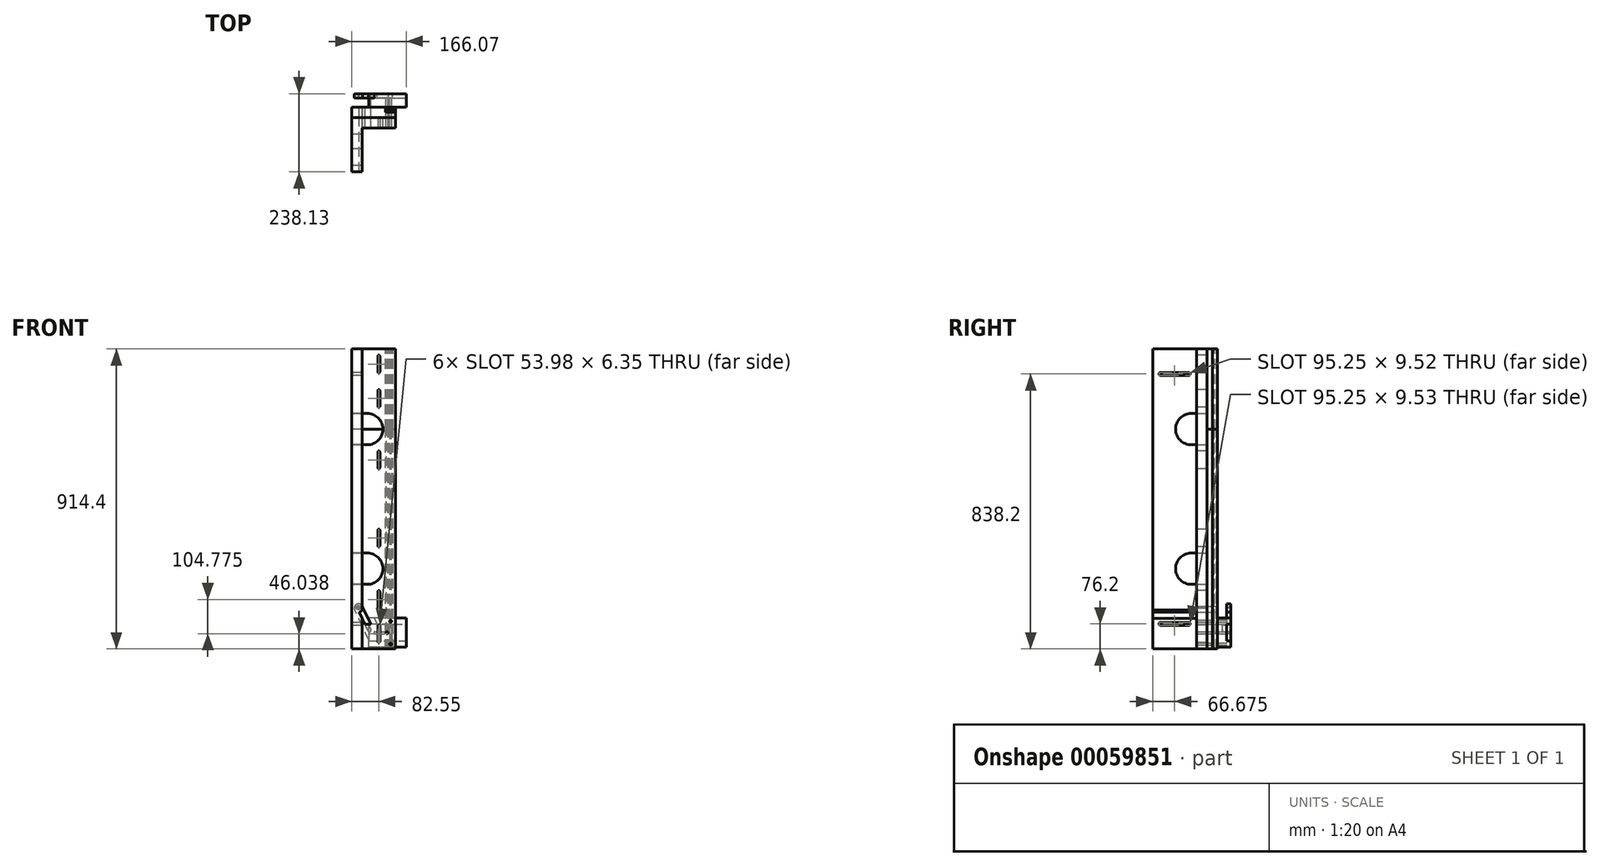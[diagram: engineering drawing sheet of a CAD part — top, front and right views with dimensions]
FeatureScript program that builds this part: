
annotation { "Feature Type Name" : "Feature", "Feature Type Description" : "" }
export const myFeature = defineFeature(function(context is Context, id is Id, definition is map)
    precondition{}
    {
        {
            var Q0;
            Q0=qCreatedBy(makeId("Top.planeOp"),FACE);
            var sketch = newSketch(context, id + "F0", { "sketchPlane" : qUnion([Q0])});
            skLineSegment(sketch, "E0", {"start": v(0, 0) * mm, "end": v(0, 165.1) * mm});
            skLineSegment(sketch, "E1", {"start": v(0, 165.1) * mm, "end": v(133.35, 165.1) * mm});
            skLineSegment(sketch, "E2.0", {"start": v(31.75, 133.35) * mm, "end": v(133.35, 133.35) * mm});
            skLineSegment(sketch, "E3.0", {"start": v(31.75, 0) * mm, "end": v(31.75, 133.35) * mm});
            skLineSegment(sketch, "E4", {"start": v(133.35, 133.35) * mm, "end": v(133.35, 165.1) * mm});
            skLineSegment(sketch, "E5", {"start": v(31.75, 0) * mm, "end": v(0, 0) * mm});
            skSolve(sketch);
        }
        {
            var Q0;
            Q0=makeQuery(id+"F0.imprint","IMPRINT",FACE,{"disambiguationData":[TD([[makeQuery(id+"F0.imprint","IMPRINT",EDGE,{"derivedFrom":sQuery(id+"F0.wireOp",EDGE,"E0")}),-1.0]])]});
            extrude(context, id + "F1", {"entities" : qUnion([Q0]), "depth" : 914.4 * mm});
        }
        {
            var Q0;
            Q0=makeQuery(id+"F1.opExtrude","SWEPT_FACE",FACE,{"disambiguationData":[OSD([sQuery(id+"F0.wireOp",EDGE,"E1")])]});
            var sketch = newSketch(context, id + "F2", { "sketchPlane" : qUnion([Q0])});
            skLineSegment(sketch, "E6", {"start": v(0, 196.85) * mm, "end": v(-47.63, 196.85) * mm});
            skLineSegment(sketch, "E7", {"start": v(0, 292.1) * mm, "end": v(-47.63, 292.1) * mm});
            skLineSegment(sketch, "E8", {"start": v(0, 196.85) * mm, "end": v(0, 292.1) * mm});
            skArc(sketch, "E9", {"start": v(-47.63, 196.85) * mm, "mid": v(-95.25, 244.48) * mm, "end": v(-47.63, 292.1) * mm});
            skLineSegment(sketch, "E10", {"start": v(0, 457.2) * mm, "end": v(-175.32, 457.2) * mm, "construction": true});
            skLineSegment(sketch, "E11.MirrorCS", {"start": v(0, 717.55) * mm, "end": v(-47.63, 717.55) * mm});
            skLineSegment(sketch, "E12.MirrorCS", {"start": v(0, 622.3) * mm, "end": v(-47.63, 622.3) * mm});
            skLineSegment(sketch, "E13.MirrorCS", {"start": v(0, 717.55) * mm, "end": v(0, 622.3) * mm});
            skArc(sketch, "E14.MirrorCS", {"start": v(-47.63, 717.55) * mm, "mid": v(-95.25, 669.93) * mm, "end": v(-47.63, 622.3) * mm});
            skSolve(sketch);
        }
        {
            var Q0;
            Q0 = qSketchRegion(id + "F2", true);
            var Q1;
            Q1=makeQuery(id+"F1.opExtrude","SWEPT_FACE",FACE,{"disambiguationData":[OSD([sQuery(id+"F0.wireOp",EDGE,"E2.0")])]});
            extrude(context, id + "F3", {"entities" : qUnion([Q0]), "operationType" : NewBodyOperationType.REMOVE, "endBound" : BoundingType.UP_TO_SURFACE, "oppositeDirection" : true, "endBoundEntityFace" : qUnion([Q1]), "depth" : 25.4 * mm});
        }
        {
            var Q0;
            Q0=makeQuery(id+"F1.opExtrude","SWEPT_FACE",FACE,{"disambiguationData":[OSD([sQuery(id+"F0.wireOp",EDGE,"E0")])]});
            var sketch = newSketch(context, id + "F4", { "sketchPlane" : qUnion([Q0])});
            skLineSegment(sketch, "E15", {"start": v(-165.1, 196.85) * mm, "end": v(-117.48, 196.85) * mm});
            skLineSegment(sketch, "E16", {"start": v(-165.1, 292.1) * mm, "end": v(-117.48, 292.1) * mm});
            skPoint(sketch, "E16.endSnap0", {"position": v(-149.22, 292.1) * mm});
            skLineSegment(sketch, "E17", {"start": v(-165.1, 196.85) * mm, "end": v(-165.1, 292.1) * mm});
            skArc(sketch, "E18", {"start": v(-117.48, 196.85) * mm, "mid": v(-69.85, 244.48) * mm, "end": v(-117.48, 292.1) * mm});
            skLineSegment(sketch, "E19", {"start": v(0, 457.2) * mm, "end": v(-264.31, 457.2) * mm, "construction": true});
            skArc(sketch, "E20.MirrorCS", {"start": v(-117.48, 717.55) * mm, "mid": v(-69.85, 669.93) * mm, "end": v(-117.48, 622.3) * mm});
            skLineSegment(sketch, "E21.MirrorCS", {"start": v(-165.1, 717.55) * mm, "end": v(-165.1, 622.3) * mm});
            skLineSegment(sketch, "E22.MirrorCS", {"start": v(-165.1, 622.3) * mm, "end": v(-117.48, 622.3) * mm});
            skLineSegment(sketch, "E23.MirrorCS", {"start": v(-165.1, 717.55) * mm, "end": v(-117.48, 717.55) * mm});
            skPoint(sketch, "E24.MirrorP", {"position": v(-149.22, 622.3) * mm});
            skSolve(sketch);
        }
        {
            var Q0;
            Q0 = qSketchRegion(id + "F4", true);
            var Q1;
            Q1=makeQuery(id+"F1.opExtrude","SWEPT_FACE",FACE,{"disambiguationData":[OSD([sQuery(id+"F0.wireOp",EDGE,"E3.0")])]});
            extrude(context, id + "F5", {"entities" : qUnion([Q0]), "operationType" : NewBodyOperationType.REMOVE, "endBound" : BoundingType.UP_TO_SURFACE, "oppositeDirection" : true, "endBoundEntityFace" : qUnion([Q1]), "depth" : 25.4 * mm});
        }
        {
            var Q0;
            Q0=makeQuery(id+"F1.opExtrude","SWEPT_FACE",FACE,{"disambiguationData":[OSD([sQuery(id+"F0.wireOp",EDGE,"E0")])]});
            var sketch = newSketch(context, id + "F6", { "sketchPlane" : qUnion([Q0])});
            skLineSegment(sketch, "E25.bottom", {"start": v(-109.54, 71.44) * mm, "end": v(-23.81, 71.44) * mm});
            skLineSegment(sketch, "E25.top", {"start": v(-109.54, 80.96) * mm, "end": v(-23.81, 80.96) * mm});
            skArc(sketch, "E26", {"start": v(-109.54, 80.96) * mm, "mid": v(-114.3, 76.2) * mm, "end": v(-109.54, 71.44) * mm});
            skArc(sketch, "E27", {"start": v(-23.81, 71.44) * mm, "mid": v(-19.05, 76.2) * mm, "end": v(-23.81, 80.96) * mm});
            skLineSegment(sketch, "E28.MirrorCS", {"start": v(-109.54, 842.96) * mm, "end": v(-23.81, 842.96) * mm});
            skLineSegment(sketch, "E29.MirrorCS", {"start": v(-109.54, 833.44) * mm, "end": v(-23.81, 833.44) * mm});
            skArc(sketch, "E30.MirrorCS", {"start": v(-109.54, 833.44) * mm, "mid": v(-114.3, 838.2) * mm, "end": v(-109.54, 842.96) * mm});
            skArc(sketch, "E31.MirrorCS", {"start": v(-23.81, 842.96) * mm, "mid": v(-19.05, 838.2) * mm, "end": v(-23.81, 833.44) * mm});
            skSolve(sketch);
        }
        {
            var Q0;
            Q0 = qSketchRegion(id + "F6", true);
            extrude(context, id + "F7", {"entities" : qUnion([Q0]), "operationType" : NewBodyOperationType.REMOVE, "endBound" : BoundingType.THROUGH_ALL, "oppositeDirection" : true, "depth" : 25.4 * mm});
        }
        {
            var Q0;
            Q0=makeQuery(id+"F1.opExtrude","SWEPT_FACE",FACE,{"disambiguationData":[OSD([sQuery(id+"F0.wireOp",EDGE,"E2.0")])]});
            var sketch = newSketch(context, id + "F8", { "sketchPlane" : qUnion([Q0])});
            skLineSegment(sketch, "E32.left", {"start": v(85.73, 22.23) * mm, "end": v(85.72, 69.85) * mm});
            skLineSegment(sketch, "E32.right", {"start": v(79.38, 22.23) * mm, "end": v(79.37, 69.85) * mm});
            skArc(sketch, "E33", {"start": v(79.38, 22.23) * mm, "mid": v(82.55, 19.05) * mm, "end": v(85.73, 22.23) * mm});
            skArc(sketch, "E34", {"start": v(85.73, 69.85) * mm, "mid": v(82.55, 73.02) * mm, "end": v(79.38, 69.85) * mm});
            skLineSegment(sketch, "E35", {"start": v(82.55, 0) * mm, "end": v(82.55, 223.18) * mm, "construction": true});
            skLineSegment(sketch, "E36", {"start": v(31.75, 98.43) * mm, "end": v(177.99, 98.43) * mm, "construction": true});
            skLineSegment(sketch, "E37.MirrorCS", {"start": v(85.73, 174.63) * mm, "end": v(85.72, 127) * mm});
            skArc(sketch, "E38.MirrorCS", {"start": v(85.73, 127) * mm, "mid": v(82.55, 123.83) * mm, "end": v(79.38, 127) * mm});
            skArc(sketch, "E39.MirrorCS", {"start": v(79.38, 174.63) * mm, "mid": v(82.55, 177.8) * mm, "end": v(85.73, 174.63) * mm});
            skLineSegment(sketch, "E40.MirrorCS", {"start": v(79.38, 174.63) * mm, "end": v(79.37, 127) * mm});
            skLineSegment(sketch, "E41", {"start": v(47.63, 244.48) * mm, "end": v(193.78, 244.47) * mm, "construction": true});
            skArc(sketch, "E42.MirrorCS", {"start": v(79.38, 314.32) * mm, "mid": v(82.55, 311.15) * mm, "end": v(85.73, 314.32) * mm});
            skArc(sketch, "E43.MirrorCS", {"start": v(85.73, 361.95) * mm, "mid": v(82.55, 365.12) * mm, "end": v(79.38, 361.95) * mm});
            skLineSegment(sketch, "E44.MirrorCS", {"start": v(79.38, 314.32) * mm, "end": v(79.38, 361.95) * mm});
            skLineSegment(sketch, "E45.MirrorCS", {"start": v(85.73, 314.32) * mm, "end": v(85.73, 361.95) * mm});
            skArc(sketch, "E46.MirrorCS", {"start": v(85.73, 787.4) * mm, "mid": v(82.55, 790.57) * mm, "end": v(79.38, 787.4) * mm});
            skArc(sketch, "E47.MirrorCS", {"start": v(85.73, 552.45) * mm, "mid": v(82.55, 549.28) * mm, "end": v(79.38, 552.45) * mm});
            skArc(sketch, "E48.MirrorCS", {"start": v(79.38, 600.08) * mm, "mid": v(82.55, 603.25) * mm, "end": v(85.73, 600.08) * mm});
            skArc(sketch, "E49.MirrorCS", {"start": v(79.38, 892.18) * mm, "mid": v(82.55, 895.35) * mm, "end": v(85.73, 892.18) * mm});
            skArc(sketch, "E50.MirrorCS", {"start": v(79.38, 739.78) * mm, "mid": v(82.55, 736.6) * mm, "end": v(85.73, 739.78) * mm});
            skArc(sketch, "E51.MirrorCS", {"start": v(85.73, 844.55) * mm, "mid": v(82.55, 841.38) * mm, "end": v(79.38, 844.55) * mm});
            skLineSegment(sketch, "E52.MirrorCS", {"start": v(79.38, 739.78) * mm, "end": v(79.37, 787.4) * mm});
            skLineSegment(sketch, "E53.MirrorCS", {"start": v(79.38, 600.08) * mm, "end": v(79.38, 552.45) * mm});
            skLineSegment(sketch, "E54.MirrorCS", {"start": v(85.73, 600.08) * mm, "end": v(85.73, 552.45) * mm});
            skLineSegment(sketch, "E55.MirrorCS", {"start": v(85.73, 892.18) * mm, "end": v(85.72, 844.55) * mm});
            skLineSegment(sketch, "E56.MirrorCS", {"start": v(79.38, 892.18) * mm, "end": v(79.37, 844.55) * mm});
            skLineSegment(sketch, "E57.MirrorCS", {"start": v(85.73, 739.78) * mm, "end": v(85.72, 787.4) * mm});
            skSolve(sketch);
        }
        {
            var Q0;
            Q0 = qSketchRegion(id + "F8", true);
            extrude(context, id + "F9", {"entities" : qUnion([Q0]), "operationType" : NewBodyOperationType.REMOVE, "endBound" : BoundingType.THROUGH_ALL, "oppositeDirection" : true, "depth" : 25.4 * mm});
        }
        {
            var Q0;
            {var subQ4=sQuery(id+"F2.wireOp",EDGE,"E6");Q0=makeQuery(id+"F2.imprint","IMPRINT",FACE,{"disambiguationData":[TD([[makeQuery(id+"F2.imprint","IMPRINT",EDGE,{"derivedFrom":subQ4}),1.0]])]});}
            var sketch = newSketch(context, id + "F10", { "sketchPlane" : qUnion([Q0])});
            skLineSegment(sketch, "E58.bottom", {"start": v(-133.35, 914.4) * mm, "end": v(0, 914.4) * mm});
            skLineSegment(sketch, "E58.top", {"start": v(-133.35, 669.93) * mm, "end": v(0, 669.93) * mm});
            skLineSegment(sketch, "E58.left", {"start": v(-133.35, 914.4) * mm, "end": v(-133.35, 669.93) * mm});
            skLineSegment(sketch, "E58.right", {"start": v(0, 914.4) * mm, "end": v(0, 669.93) * mm});
            skSolve(sketch);
        }
        {
            var Q0;
            Q0 = qSketchRegion(id + "F10", true);
            extrude(context, id + "F11", {"entities" : qUnion([Q0]), "depth" : 31.75 * mm});
        }
        {
            var Q0;
            {var subQ4=sQuery(id+"F2.wireOp",EDGE,"E6");Q0=makeQuery(id+"F2.imprint","IMPRINT",FACE,{"disambiguationData":[TD([[makeQuery(id+"F2.imprint","IMPRINT",EDGE,{"derivedFrom":subQ4}),1.0]])]});}
            var sketch = newSketch(context, id + "F12", { "sketchPlane" : qUnion([Q0])});
            skLineSegment(sketch, "E59.bottom", {"start": v(-133.35, 669.93) * mm, "end": v(0, 669.93) * mm});
            skLineSegment(sketch, "E59.top", {"start": v(-133.35, 0) * mm, "end": v(0, 0) * mm});
            skLineSegment(sketch, "E59.left", {"start": v(-133.35, 669.93) * mm, "end": v(-133.35, 0) * mm});
            skLineSegment(sketch, "E59.right", {"start": v(0, 669.93) * mm, "end": v(0, 0) * mm});
            skSolve(sketch);
        }
        {
            var Q0;
            Q0 = qSketchRegion(id + "F12", true);
            extrude(context, id + "F13", {"entities" : qUnion([Q0]), "depth" : 31.75 * mm});
        }
        {
            var Q0;
            Q0=makeQuery(id+"F11.opExtrude","SWEPT_FACE",FACE,{"disambiguationData":[OSD([sQuery(id+"F10.wireOp",EDGE,"E58.bottom")])]});
            var sketch = newSketch(context, id + "F14", { "sketchPlane" : qUnion([Q0])});
            skLineSegment(sketch, "E60.bottom", {"start": v(133.35, 196.85) * mm, "end": v(103.53, 196.85) * mm});
            skLineSegment(sketch, "E60.top", {"start": v(133.35, 182.14) * mm, "end": v(103.53, 182.14) * mm});
            skLineSegment(sketch, "E60.left", {"start": v(133.35, 196.85) * mm, "end": v(133.35, 182.14) * mm});
            skLineSegment(sketch, "E60.right", {"start": v(103.53, 196.85) * mm, "end": v(103.53, 182.14) * mm});
            skSolve(sketch);
        }
        {
            var Q0;
            Q0 = qSketchRegion(id + "F14", true);
            extrude(context, id + "F15", {"entities" : qUnion([Q0]), "operationType" : NewBodyOperationType.REMOVE, "endBound" : BoundingType.THROUGH_ALL, "oppositeDirection" : true, "depth" : 25.4 * mm});
        }
        {
            var Q0;
            Q0=makeQuery(id+"F13.opExtrude","SWEPT_FACE",FACE,{"disambiguationData":[OSD([sQuery(id+"F12.wireOp",EDGE,"E59.bottom")])]});
            var sketch = newSketch(context, id + "F16", { "sketchPlane" : qUnion([Q0])});
            skLineSegment(sketch, "E61.bottom", {"start": v(133.35, 196.85) * mm, "end": v(103.53, 196.85) * mm});
            skLineSegment(sketch, "E61.top", {"start": v(133.35, 182.14) * mm, "end": v(103.53, 182.14) * mm});
            skLineSegment(sketch, "E61.left", {"start": v(133.35, 196.85) * mm, "end": v(133.35, 182.14) * mm});
            skLineSegment(sketch, "E61.right", {"start": v(103.53, 196.85) * mm, "end": v(103.53, 182.14) * mm});
            skSolve(sketch);
        }
        {
            var Q0;
            Q0 = qSketchRegion(id + "F16", true);
            extrude(context, id + "F17", {"entities" : qUnion([Q0]), "operationType" : NewBodyOperationType.REMOVE, "endBound" : BoundingType.THROUGH_ALL, "oppositeDirection" : true, "depth" : 25.4 * mm});
        }
        {
            var Q0;
            Q0=makeQuery(id+"F11.opExtrude","SWEPT_FACE",FACE,{"disambiguationData":[OSD([sQuery(id+"F10.wireOp",EDGE,"E58.bottom")])]});
            var sketch = newSketch(context, id + "F18", { "sketchPlane" : qUnion([Q0])});
            skLineSegment(sketch, "E62", {"start": v(133.35, 182.14) * mm, "end": v(103.53, 182.14) * mm});
            skLineSegment(sketch, "E63", {"start": v(103.53, 182.14) * mm, "end": v(103.53, 196.85) * mm});
            skLineSegment(sketch, "E64", {"start": v(103.53, 196.85) * mm, "end": v(115.27, 196.85) * mm});
            skLineSegment(sketch, "E65", {"start": v(115.27, 196.85) * mm, "end": v(115.27, 195.07) * mm});
            skLineSegment(sketch, "E66", {"start": v(115.27, 195.07) * mm, "end": v(112.73, 195.07) * mm});
            skLineSegment(sketch, "E67", {"start": v(112.73, 195.07) * mm, "end": v(112.73, 188.72) * mm});
            skLineSegment(sketch, "E68", {"start": v(112.73, 188.72) * mm, "end": v(124.16, 188.72) * mm});
            skLineSegment(sketch, "E69", {"start": v(124.16, 188.72) * mm, "end": v(124.16, 195.07) * mm});
            skLineSegment(sketch, "E70", {"start": v(124.16, 195.07) * mm, "end": v(121.62, 195.07) * mm});
            skLineSegment(sketch, "E71", {"start": v(121.62, 195.07) * mm, "end": v(121.62, 196.85) * mm});
            skLineSegment(sketch, "E72", {"start": v(121.62, 196.85) * mm, "end": v(133.35, 196.85) * mm});
            skLineSegment(sketch, "E73", {"start": v(133.35, 196.85) * mm, "end": v(133.35, 182.14) * mm});
            skLineSegment(sketch, "E74", {"start": v(116.66, 183.92) * mm, "end": v(116.66, 186.94) * mm});
            skLineSegment(sketch, "E75", {"start": v(116.66, 186.94) * mm, "end": v(110.95, 186.94) * mm});
            skLineSegment(sketch, "E76", {"start": v(110.95, 186.94) * mm, "end": v(110.95, 195.07) * mm});
            skLineSegment(sketch, "E77", {"start": v(110.95, 195.07) * mm, "end": v(105.3, 195.07) * mm});
            skLineSegment(sketch, "E78", {"start": v(105.3, 195.07) * mm, "end": v(105.3, 183.92) * mm});
            skLineSegment(sketch, "E79", {"start": v(105.3, 183.92) * mm, "end": v(116.66, 183.92) * mm});
            skLineSegment(sketch, "E80", {"start": v(118.44, 182.14) * mm, "end": v(118.44, 192.35) * mm, "construction": true});
            skLineSegment(sketch, "E81.MirrorCS", {"start": v(120.22, 183.92) * mm, "end": v(120.22, 186.94) * mm});
            skLineSegment(sketch, "E82.MirrorCS", {"start": v(120.22, 186.94) * mm, "end": v(125.93, 186.94) * mm});
            skLineSegment(sketch, "E83.MirrorCS", {"start": v(131.57, 183.92) * mm, "end": v(120.22, 183.92) * mm});
            skLineSegment(sketch, "E84.MirrorCS", {"start": v(125.93, 186.94) * mm, "end": v(125.93, 195.07) * mm});
            skLineSegment(sketch, "E85.MirrorCS", {"start": v(131.57, 195.07) * mm, "end": v(131.57, 183.92) * mm});
            skLineSegment(sketch, "E86.MirrorCS", {"start": v(125.93, 195.07) * mm, "end": v(131.57, 195.07) * mm});
            skSolve(sketch);
        }
        {
            var Q0;
            Q0=makeQuery(id+"F18.imprint","IMPRINT",FACE,{"disambiguationData":[TD([[makeQuery(id+"F18.imprint","IMPRINT",EDGE,{"derivedFrom":sQuery(id+"F18.wireOp",EDGE,"E62")}),-1.0]])]});
            var Q1;
            Q1=makeQuery(id+"F11.opExtrude","SWEPT_FACE",FACE,{"disambiguationData":[OSD([sQuery(id+"F10.wireOp",EDGE,"E58.top")])]});
            extrude(context, id + "F19", {"entities" : qUnion([Q0]), "endBound" : BoundingType.UP_TO_SURFACE, "oppositeDirection" : true, "endBoundEntityFace" : qUnion([Q1]), "depth" : 79.93 * mm});
        }
        {
            var Q0;
            Q0=makeQuery(id+"F13.opExtrude","SWEPT_FACE",FACE,{"disambiguationData":[OSD([sQuery(id+"F12.wireOp",EDGE,"E59.bottom")])]});
            var sketch = newSketch(context, id + "F20", { "sketchPlane" : qUnion([Q0])});
            skLineSegment(sketch, "E87", {"start": v(133.35, 182.14) * mm, "end": v(103.53, 182.14) * mm});
            skLineSegment(sketch, "E88", {"start": v(103.53, 182.14) * mm, "end": v(103.53, 196.85) * mm});
            skLineSegment(sketch, "E89", {"start": v(103.53, 196.85) * mm, "end": v(115.27, 196.85) * mm});
            skLineSegment(sketch, "E90", {"start": v(115.27, 196.85) * mm, "end": v(115.27, 195.07) * mm});
            skLineSegment(sketch, "E91", {"start": v(115.27, 195.07) * mm, "end": v(112.73, 195.07) * mm});
            skLineSegment(sketch, "E92", {"start": v(112.73, 195.07) * mm, "end": v(112.73, 188.72) * mm});
            skLineSegment(sketch, "E93", {"start": v(112.73, 188.72) * mm, "end": v(124.16, 188.72) * mm});
            skLineSegment(sketch, "E94", {"start": v(124.16, 188.72) * mm, "end": v(124.16, 195.07) * mm});
            skLineSegment(sketch, "E95", {"start": v(124.16, 195.07) * mm, "end": v(121.62, 195.07) * mm});
            skLineSegment(sketch, "E96", {"start": v(121.62, 195.07) * mm, "end": v(121.62, 196.85) * mm});
            skLineSegment(sketch, "E97", {"start": v(121.62, 196.85) * mm, "end": v(133.35, 196.85) * mm});
            skLineSegment(sketch, "E98", {"start": v(133.35, 196.85) * mm, "end": v(133.35, 182.14) * mm});
            skLineSegment(sketch, "E99", {"start": v(116.66, 183.92) * mm, "end": v(116.66, 186.94) * mm});
            skLineSegment(sketch, "E100", {"start": v(116.66, 186.94) * mm, "end": v(110.95, 186.94) * mm});
            skLineSegment(sketch, "E101", {"start": v(110.95, 186.94) * mm, "end": v(110.95, 195.07) * mm});
            skLineSegment(sketch, "E102", {"start": v(110.95, 195.07) * mm, "end": v(105.3, 195.07) * mm});
            skLineSegment(sketch, "E103", {"start": v(105.3, 195.07) * mm, "end": v(105.3, 183.92) * mm});
            skLineSegment(sketch, "E104", {"start": v(105.3, 183.92) * mm, "end": v(116.66, 183.92) * mm});
            skLineSegment(sketch, "E105", {"start": v(118.44, 182.14) * mm, "end": v(118.44, 192.35) * mm, "construction": true});
            skLineSegment(sketch, "E106.MirrorCS", {"start": v(120.22, 183.92) * mm, "end": v(120.22, 186.94) * mm});
            skLineSegment(sketch, "E107.MirrorCS", {"start": v(120.22, 186.94) * mm, "end": v(125.93, 186.94) * mm});
            skLineSegment(sketch, "E108.MirrorCS", {"start": v(131.57, 183.92) * mm, "end": v(120.22, 183.92) * mm});
            skLineSegment(sketch, "E109.MirrorCS", {"start": v(125.93, 186.94) * mm, "end": v(125.93, 195.07) * mm});
            skLineSegment(sketch, "E110.MirrorCS", {"start": v(131.57, 195.07) * mm, "end": v(131.57, 183.92) * mm});
            skLineSegment(sketch, "E111.MirrorCS", {"start": v(125.93, 195.07) * mm, "end": v(131.57, 195.07) * mm});
            skSolve(sketch);
        }
        {
            var Q0;
            Q0 = qSketchRegion(id + "F20", true);
            var Q1;
            Q1=makeQuery(id+"F13.opExtrude","SWEPT_FACE",FACE,{"disambiguationData":[OSD([sQuery(id+"F12.wireOp",EDGE,"E59.top")])]});
            extrude(context, id + "F21", {"entities" : qUnion([Q0]), "endBound" : BoundingType.UP_TO_SURFACE, "oppositeDirection" : true, "endBoundEntityFace" : qUnion([Q1]), "depth" : 25.4 * mm});
        }
        {
            var Q0;
            Q0=makeQuery(id+"F21.opExtrude","SWEPT_FACE",FACE,{"disambiguationData":[OSD([sQuery(id+"F20.wireOp",EDGE,"E98")])]});
            cPlane(context, id + "F22", {"entities" : qUnion([Q0]), "cplaneType" : CPlaneType.OFFSET, "offset" : 14.9 * mm, "oppositeDirection" : true, "width" : 152.4 * mm, "height" : 152.4 * mm});
        }
        {
            var Q0;
            Q0=makeQuery(id+"F13.opExtrude","CAP_FACE",FACE,{"disambiguationData":[OSD([sQuery(id+"F12.wireOp",EDGE,"E59.bottom"),sQuery(id+"F12.wireOp",EDGE,"E59.top"),sQuery(id+"F12.wireOp",EDGE,"E59.left"),sQuery(id+"F12.wireOp",EDGE,"E59.right")])],"isStart":false});
            var sketch = newSketch(context, id + "F23", { "sketchPlane" : qUnion([Q0])});
            skLineSegment(sketch, "E112.bottom", {"start": v(-166.07, 4.91) * mm, "end": v(-51.77, 4.91) * mm});
            skLineSegment(sketch, "E112.top", {"start": v(-166.07, 93.81) * mm, "end": v(-51.77, 93.81) * mm});
            skLineSegment(sketch, "E112.left", {"start": v(-166.07, 4.91) * mm, "end": v(-166.07, 93.81) * mm});
            skLineSegment(sketch, "E112.right", {"start": v(-51.77, 4.91) * mm, "end": v(-51.77, 93.81) * mm});
            skSolve(sketch);
        }
        {
            var Q0;
            {var subQ0=sQuery(id+"F23.wireOp",EDGE,"E112.left");Q0=makeQuery(id+"F23.imprint","IMPRINT",FACE,{"disambiguationData":[TD([[makeQuery(id+"F23.imprint","IMPRINT",EDGE,{"derivedFrom":subQ0}),-1.0]])]});}
            var Q1;
            {var subQ0=sQuery(id+"F23.wireOp",EDGE,"E112.right");Q1=makeQuery(id+"F23.imprint","IMPRINT",FACE,{"disambiguationData":[TD([[makeQuery(id+"F23.imprint","IMPRINT",EDGE,{"derivedFrom":subQ0}),1.0]])]});}
            extrude(context, id + "F24", {"entities" : qUnion([Q0, Q1]), "depth" : 41.27 * mm});
        }
        {
            var Q0;
            Q0=makeQuery(id+"F24.opExtrude","SWEPT_FACE",FACE,{"disambiguationData":[OSD([sQuery(id+"F23.wireOp",EDGE,"E112.left")])]});
            var sketch = newSketch(context, id + "F25", { "sketchPlane" : qUnion([Q0])});
            skLineSegment(sketch, "E113.top", {"start": v(238.13, 23.96) * mm, "end": v(225.43, 23.96) * mm});
            skLineSegment(sketch, "E113.right", {"start": v(225.43, 74.76) * mm, "end": v(225.43, 23.96) * mm});
            skPoint(sketch, "E114.endSnap0", {"position": v(217.49, 93.81) * mm});
            skLineSegment(sketch, "E115", {"start": v(225.43, 74.76) * mm, "end": v(238.13, 74.76) * mm});
            skLineSegment(sketch, "E116", {"start": v(238.13, 49.36) * mm, "end": v(214.84, 49.36) * mm, "construction": true});
            skPoint(sketch, "E116.endSnap0", {"position": v(238.13, 49.36) * mm});
            skLineSegment(sketch, "E117", {"start": v(214.84, 49.36) * mm, "end": v(228.34, 49.36) * mm});
            skLineSegment(sketch, "E118", {"start": v(238.13, 23.96) * mm, "end": v(238.13, 49.36) * mm});
            skLineSegment(sketch, "E119", {"start": v(238.13, 74.76) * mm, "end": v(238.13, 49.36) * mm});
            skSolve(sketch);
        }
        {
            var Q0;
            Q0 = qSketchRegion(id + "F25", true);
            extrude(context, id + "F26", {"entities" : qUnion([Q0]), "operationType" : NewBodyOperationType.REMOVE, "endBound" : BoundingType.THROUGH_ALL, "oppositeDirection" : true, "depth" : 25.4 * mm});
        }
        {
            var Q0;
            Q0=makeQuery(id+"F24.opExtrude","CAP_FACE",FACE,{"disambiguationData":[OSD([sQuery(id+"F23.wireOp",EDGE,"E112.bottom"),sQuery(id+"F23.wireOp",EDGE,"E112.top"),sQuery(id+"F23.wireOp",EDGE,"E112.left"),sQuery(id+"F23.wireOp",EDGE,"E112.right")])],"isStart":false});
            var sketch = newSketch(context, id + "F27", { "sketchPlane" : qUnion([Q0])});
            skPoint(sketch, "E120.endSnap0", {"position": v(-51.77, 14.44) * mm});
            skCircle(sketch, "E121.MirrorC", {"center": v(-118.44, 14.44) * mm, "radius": 3.18 * mm});
            skLineSegment(sketch, "E122", {"start": v(-166.07, 14.44) * mm, "end": v(-75.74, 14.44) * mm, "construction": true});
            skPoint(sketch, "E122.endSnap0", {"position": v(-166.07, 14.44) * mm});
            skPoint(sketch, "E123.endSnap0", {"position": v(-108.92, 23.96) * mm});
            skSolve(sketch);
        }
        {
            var Q0;
            Q0 = qSketchRegion(id + "F27", true);
            extrude(context, id + "F28", {"entities" : qUnion([Q0]), "operationType" : NewBodyOperationType.REMOVE, "endBound" : BoundingType.THROUGH_ALL, "oppositeDirection" : true, "depth" : 25.4 * mm});
        }
        {
            var Q0;
            {var subQ0=sQuery(id+"F23.wireOp",EDGE,"E112.top");var subQ1=sQuery(id+"F23.wireOp",EDGE,"E112.left");var subQ2=sQuery(id+"F23.wireOp",EDGE,"E112.right");Q0=makeQuery(id+"F26.boolean.opBoolean","SPLIT",FACE,{"disambiguationData":[TD([makeQuery(id+"F24.opExtrude","SWEPT_FACE",FACE,{"disambiguationData":[OSD([subQ0])]})])],"derivedFrom":makeQuery(id+"F24.opExtrude","CAP_FACE",FACE,{"disambiguationData":[OSD([sQuery(id+"F23.wireOp",EDGE,"E112.bottom"),subQ0,subQ1,subQ2])],"isStart":false})});}
            var sketch = newSketch(context, id + "F29", { "sketchPlane" : qUnion([Q0])});
            skCircle(sketch, "E124", {"center": v(-118.44, 84.29) * mm, "radius": 3.18 * mm});
            skLineSegment(sketch, "E125", {"start": v(-166.07, 84.29) * mm, "end": v(-102.12, 84.29) * mm, "construction": true});
            skLineSegment(sketch, "E126", {"start": v(-121.62, 0.6) * mm, "end": v(-121.62, 113.24) * mm, "construction": true});
            skSolve(sketch);
        }
        {
            var Q0;
            Q0 = qSketchRegion(id + "F29", true);
            extrude(context, id + "F30", {"entities" : qUnion([Q0]), "operationType" : NewBodyOperationType.REMOVE, "endBound" : BoundingType.THROUGH_ALL, "oppositeDirection" : true, "depth" : 25.4 * mm});
        }
        {
            var Q0;
            {var subQ0=sQuery(id+"F23.wireOp",EDGE,"E112.top");var subQ1=sQuery(id+"F23.wireOp",EDGE,"E112.right");var subQ2=sQuery(id+"F23.wireOp",EDGE,"E112.left");Q0=makeQuery(id+"F26.boolean.opBoolean","SPLIT",FACE,{"disambiguationData":[TD([makeQuery(id+"F24.opExtrude","SWEPT_FACE",FACE,{"disambiguationData":[OSD([subQ0])]})])],"derivedFrom":makeQuery(id+"F24.opExtrude","CAP_FACE",FACE,{"disambiguationData":[OSD([sQuery(id+"F23.wireOp",EDGE,"E112.bottom"),subQ0,subQ2,subQ1])],"isStart":false})});}
            var sketch = newSketch(context, id + "F31", { "sketchPlane" : qUnion([Q0])});
            skLineSegment(sketch, "E127", {"start": v(-51.77, 93.81) * mm, "end": v(-68.6, 93.81) * mm});
            skLineSegment(sketch, "E128", {"start": v(-68.6, 93.81) * mm, "end": v(-77.48, 74.76) * mm});
            skLineSegment(sketch, "E129", {"start": v(-77.48, 74.76) * mm, "end": v(-51.77, 74.76) * mm});
            skLineSegment(sketch, "E130", {"start": v(-51.77, 74.76) * mm, "end": v(-51.77, 93.81) * mm});
            skSolve(sketch);
        }
        {
            var Q0;
            Q0 = qSketchRegion(id + "F31", true);
            var Q1;
            Q1=makeQuery(id+"F26.boolean.opBoolean","COPY",FACE,{"derivedFrom":makeQuery(id+"F26.opExtrude","SWEPT_FACE",FACE,{"disambiguationData":[OSD([sQuery(id+"F25.wireOp",EDGE,"E113.right")])]})});
            extrude(context, id + "F32", {"entities" : qUnion([Q0]), "operationType" : NewBodyOperationType.REMOVE, "endBound" : BoundingType.UP_TO_SURFACE, "oppositeDirection" : true, "endBoundEntityFace" : qUnion([Q1]), "depth" : 2.54 * mm});
        }
        {
            var Q0;
            Q0=makeQuery(id+"F26.boolean.opBoolean","COPY",FACE,{"derivedFrom":makeQuery(id+"F26.opExtrude","SWEPT_FACE",FACE,{"disambiguationData":[OSD([sQuery(id+"F25.wireOp",EDGE,"E113.right")])]})});
            var sketch = newSketch(context, id + "F33", { "sketchPlane" : qUnion([Q0])});
            skLineSegment(sketch, "E131", {"start": v(-53.64, 23.96) * mm, "end": v(-9.11, 119.46) * mm});
            skLineSegment(sketch, "E132", {"start": v(-32.13, 130.2) * mm, "end": v(-57.98, 74.76) * mm});
            skLineSegment(sketch, "E133", {"start": v(-57.98, 23.96) * mm, "end": v(-123.5, 23.96) * mm});
            skLineSegment(sketch, "E134", {"start": v(-123.5, 23.96) * mm, "end": v(-123.5, 23.96) * mm});
            skLineSegment(sketch, "E135", {"start": v(-123.5, 23.96) * mm, "end": v(-53.64, 23.96) * mm});
            skArc(sketch, "E136.filletArc", {"start": v(-9.11, 119.46) * mm, "mid": v(-15.26, 136.34) * mm, "end": v(-32.13, 130.2) * mm});
            skLineSegment(sketch, "E137", {"start": v(-7.92, 104.1) * mm, "end": v(-7.92, 179.03) * mm, "construction": true});
            skLineSegment(sketch, "E138", {"start": v(-123.5, 23.96) * mm, "end": v(-123.5, 74.76) * mm});
            skLineSegment(sketch, "E139", {"start": v(-123.5, 74.76) * mm, "end": v(-57.98, 74.76) * mm});
            skSolve(sketch);
        }
        {
            var Q0;
            Q0 = qSketchRegion(id + "F33", true);
            extrude(context, id + "F34", {"entities" : qUnion([Q0]), "depth" : 12.7 * mm});
        }
        {
            var Q0;
            Q0=makeQuery(id+"F34.opExtrude","CAP_FACE",FACE,{"disambiguationData":[OSD([sQuery(id+"F33.wireOp",EDGE,"E131"),sQuery(id+"F33.wireOp",EDGE,"E132"),sQuery(id+"F33.wireOp",EDGE,"E133"),sQuery(id+"F33.wireOp",EDGE,"E134"),sQuery(id+"F33.wireOp",EDGE,"E135"),sQuery(id+"F33.wireOp",EDGE,"E136.filletArc"),sQuery(id+"F33.wireOp",EDGE,"E136.filletArc")])],"isStart":false});
            var sketch = newSketch(context, id + "F35", { "sketchPlane" : qUnion([Q0])});
            skLineSegment(sketch, "E140", {"start": v(-40.47, 74.76) * mm, "end": v(-22.94, 112.34) * mm});
            skArc(sketch, "E141", {"start": v(-32.13, 130.2) * mm, "mid": v(-31.92, 119.01) * mm, "end": v(-22.94, 112.34) * mm});
            skLineSegment(sketch, "E142", {"start": v(-32.13, 130.2) * mm, "end": v(-57.98, 74.76) * mm});
            skLineSegment(sketch, "E143", {"start": v(-57.98, 74.76) * mm, "end": v(-40.47, 74.76) * mm});
            skSolve(sketch);
        }
        {
            var Q0;
            Q0 = qSketchRegion(id + "F35", true);
            extrude(context, id + "F36", {"entities" : qUnion([Q0]), "operationType" : NewBodyOperationType.REMOVE, "endBound" : BoundingType.THROUGH_ALL, "oppositeDirection" : true, "depth" : 25.4 * mm});
        }
        {
            var Q0;
            Q0=makeQuery(id+"F34.opExtrude","CAP_FACE",FACE,{"disambiguationData":[OSD([sQuery(id+"F33.wireOp",EDGE,"E131"),sQuery(id+"F33.wireOp",EDGE,"E132"),sQuery(id+"F33.wireOp",EDGE,"E133"),sQuery(id+"F33.wireOp",EDGE,"E134"),sQuery(id+"F33.wireOp",EDGE,"E135"),sQuery(id+"F33.wireOp",EDGE,"E136.filletArc"),sQuery(id+"F33.wireOp",EDGE,"E136.filletArc")])],"isStart":true});
            var sketch = newSketch(context, id + "F37", { "sketchPlane" : qUnion([Q0])});
            skLineSegment(sketch, "E144", {"start": v(123.5, 49.36) * mm, "end": v(41.8, 49.36) * mm, "construction": true});
            skLineSegment(sketch, "E145.rect.bottom", {"start": v(107.62, 52.54) * mm, "end": v(70.38, 52.54) * mm});
            skLineSegment(sketch, "E145.rect.top", {"start": v(107.62, 46.19) * mm, "end": v(70.38, 46.19) * mm});
            skPoint(sketch, "E145.rect.middle", {"position": v(115.25, 157.16) * mm});
            skArc(sketch, "E146", {"start": v(107.62, 46.19) * mm, "mid": v(110.8, 49.36) * mm, "end": v(107.62, 52.54) * mm});
            skArc(sketch, "E147", {"start": v(70.38, 52.54) * mm, "mid": v(67.2, 49.36) * mm, "end": v(70.38, 46.19) * mm});
            skSolve(sketch);
        }
        {
            var Q0;
            Q0 = qSketchRegion(id + "F37", true);
            extrude(context, id + "F38", {"entities" : qUnion([Q0]), "operationType" : NewBodyOperationType.REMOVE, "endBound" : BoundingType.THROUGH_ALL, "oppositeDirection" : true, "depth" : 25.4 * mm});
        }
        {
            var Q0;
            Q0=makeQuery(id+"F34.opExtrude","CAP_FACE",FACE,{"disambiguationData":[OSD([sQuery(id+"F33.wireOp",EDGE,"E131"),sQuery(id+"F33.wireOp",EDGE,"E132"),sQuery(id+"F33.wireOp",EDGE,"E133"),sQuery(id+"F33.wireOp",EDGE,"E134"),sQuery(id+"F33.wireOp",EDGE,"E135"),sQuery(id+"F33.wireOp",EDGE,"E136.filletArc"),sQuery(id+"F33.wireOp",EDGE,"E136.filletArc")])],"isStart":true});
            var sketch = newSketch(context, id + "F39", { "sketchPlane" : qUnion([Q0])});
            skLineSegment(sketch, "E148", {"start": v(-4.15, 124.83) * mm, "end": v(51.88, 124.83) * mm, "construction": true});
            skSolve(sketch);
        }
        {
            var Q0;
            Q0=sQuery(id+"F39.wireOp",EDGE,"E148");
            cPlane(context, id + "F40", {"entities" : qUnion([Q0]), "cplaneType" : CPlaneType.LINE_ANGLE, "offset" : 152.4 * mm, "angle" : 5 * degree, "width" : 152.4 * mm, "height" : 152.4 * mm});
        }
        {
            var Q0;
            Q0=qCreatedBy(id+"F40.planeOp",FACE);
            var sketch = newSketch(context, id + "F41", { "sketchPlane" : qUnion([Q0])});
            skLineSegment(sketch, "E149", {"start": v(-20.62, 141.23) * mm, "end": v(-20.62, 123.39) * mm, "construction": true});
            skCircle(sketch, "E150", {"center": v(-20.62, 104.7) * mm, "radius": 4.78 * mm});
            skSolve(sketch);
        }
        {
            var Q0;
            Q0=makeQuery(id+"F41.imprint","IMPRINT",FACE,{"disambiguationData":[TD([[makeQuery(id+"F41.imprint","IMPRINT",EDGE,{"derivedFrom":sQuery(id+"F41.wireOp",EDGE,"E150")}),1.0]])]});
            var Q1;
            Q1=makeQuery(id+"F34.opExtrude","CAP_FACE",FACE,{"disambiguationData":[OSD([sQuery(id+"F33.wireOp",EDGE,"E131"),sQuery(id+"F33.wireOp",EDGE,"E132"),sQuery(id+"F33.wireOp",EDGE,"E133"),sQuery(id+"F33.wireOp",EDGE,"E134"),sQuery(id+"F33.wireOp",EDGE,"E135"),sQuery(id+"F33.wireOp",EDGE,"E136.filletArc"),sQuery(id+"F33.wireOp",EDGE,"E136.filletArc")])],"isStart":true});
            extrude(context, id + "F42", {"entities" : qUnion([Q0]), "operationType" : NewBodyOperationType.REMOVE, "depth" : 0.8 * mm, "hasSecondDirection" : true, "secondDirectionBound" : SecondDirectionBoundingType.UP_TO_SURFACE, "secondDirectionOppositeDirection" : true, "secondDirectionBoundEntityFace" : qUnion([Q1]), "secondDirectionDepth" : 25.4 * mm});
        }
        {
            var Q0;
            Q0=qCreatedBy(id+"F40.planeOp",FACE);
            var sketch = newSketch(context, id + "F43", { "sketchPlane" : qUnion([Q0])});
            skCircle(sketch, "E151", {"center": v(-20.62, 104.7) * mm, "radius": 1.47 * mm});
            skSolve(sketch);
        }
        {
            var Q0;
            Q0=makeQuery(id+"F43.imprint","IMPRINT",FACE,{"disambiguationData":[TD([[makeQuery(id+"F43.imprint","IMPRINT",EDGE,{"derivedFrom":sQuery(id+"F43.wireOp",EDGE,"E151")}),1.0]])]});
            extrude(context, id + "F44", {"entities" : qUnion([Q0]), "operationType" : NewBodyOperationType.REMOVE, "endBound" : BoundingType.THROUGH_ALL, "depth" : 25.4 * mm});
        }
        {
            var Q0;
            Q0=makeQuery(id+"F34.opExtrude","CAP_FACE",FACE,{"disambiguationData":[OSD([sQuery(id+"F33.wireOp",EDGE,"E131"),sQuery(id+"F33.wireOp",EDGE,"E132"),sQuery(id+"F33.wireOp",EDGE,"E133"),sQuery(id+"F33.wireOp",EDGE,"E134"),sQuery(id+"F33.wireOp",EDGE,"E135"),sQuery(id+"F33.wireOp",EDGE,"E136.filletArc"),sQuery(id+"F33.wireOp",EDGE,"E136.filletArc")])],"isStart":false});
            var sketch = newSketch(context, id + "F45", { "sketchPlane" : qUnion([Q0])});
            skLineSegment(sketch, "E152", {"start": v(-19.16, 125.94) * mm, "end": v(-3.45, 125.94) * mm, "construction": true});
            skPoint(sketch, "E152.endSnap0", {"position": v(-19.16, 125.94) * mm});
            skSolve(sketch);
        }
        {
            var Q0;
            Q0=sQuery(id+"F45.wireOp",EDGE,"E152");
            cPlane(context, id + "F46", {"entities" : qUnion([Q0]), "cplaneType" : CPlaneType.LINE_ANGLE, "offset" : 152.4 * mm, "angle" : 175 * degree, "width" : 152.4 * mm, "height" : 152.4 * mm});
        }
        {
            var Q0;
            Q0=qCreatedBy(id+"F46.planeOp",FACE);
            var sketch = newSketch(context, id + "F47", { "sketchPlane" : qUnion([Q0])});
            skCircle(sketch, "E153", {"center": v(-20.62, 104.7) * mm, "radius": 6.35 * mm});
            skSolve(sketch);
        }
        {
            var Q0;
            Q0=makeQuery(id+"F47.imprint","IMPRINT",FACE,{"disambiguationData":[TD([[makeQuery(id+"F47.imprint","IMPRINT",EDGE,{"derivedFrom":sQuery(id+"F47.wireOp",EDGE,"E153")}),1.0]])]});
            var Q1;
            Q1=makeQuery(id+"F34.opExtrude","CAP_FACE",FACE,{"disambiguationData":[OSD([sQuery(id+"F33.wireOp",EDGE,"E131"),sQuery(id+"F33.wireOp",EDGE,"E132"),sQuery(id+"F33.wireOp",EDGE,"E133"),sQuery(id+"F33.wireOp",EDGE,"E134"),sQuery(id+"F33.wireOp",EDGE,"E135"),sQuery(id+"F33.wireOp",EDGE,"E136.filletArc"),sQuery(id+"F33.wireOp",EDGE,"E136.filletArc")])],"isStart":false});
            extrude(context, id + "F48", {"entities" : qUnion([Q0]), "operationType" : NewBodyOperationType.REMOVE, "oppositeDirection" : true, "depth" : 0.8 * mm, "hasSecondDirection" : true, "secondDirectionBound" : SecondDirectionBoundingType.UP_TO_SURFACE, "secondDirectionOppositeDirection" : false, "secondDirectionBoundEntityFace" : qUnion([Q1]), "secondDirectionDepth" : 25.4 * mm});
        }
        {
            var Q0;
            Q0=makeQuery(id+"F34.opExtrude","CAP_FACE",FACE,{"disambiguationData":[OSD([sQuery(id+"F33.wireOp",EDGE,"E131"),sQuery(id+"F33.wireOp",EDGE,"E132"),sQuery(id+"F33.wireOp",EDGE,"E133"),sQuery(id+"F33.wireOp",EDGE,"E134"),sQuery(id+"F33.wireOp",EDGE,"E135"),sQuery(id+"F33.wireOp",EDGE,"E136.filletArc"),sQuery(id+"F33.wireOp",EDGE,"E136.filletArc")])],"isStart":false});
            var sketch = newSketch(context, id + "F49", { "sketchPlane" : qUnion([Q0])});
            skLineSegment(sketch, "E154", {"start": v(-40.47, 74.76) * mm, "end": v(-49.72, 54.92) * mm});
            skLineSegment(sketch, "E155", {"start": v(-58.35, 58.94) * mm, "end": v(-50.98, 74.76) * mm});
            skLineSegment(sketch, "E156", {"start": v(-50.98, 74.76) * mm, "end": v(-40.47, 74.76) * mm});
            skArc(sketch, "E157", {"start": v(-49.72, 54.92) * mm, "mid": v(-56.05, 52.61) * mm, "end": v(-58.35, 58.94) * mm});
            skSolve(sketch);
        }
        {
            var Q0;
            Q0 = qSketchRegion(id + "F49", true);
            extrude(context, id + "F50", {"entities" : qUnion([Q0]), "operationType" : NewBodyOperationType.REMOVE, "oppositeDirection" : true, "depth" : 25.4 * mm});
        }
        {
            var Q0;
            Q0=makeQuery(id+"F26.boolean.opBoolean","COPY",FACE,{"derivedFrom":makeQuery(id+"F26.opExtrude","SWEPT_FACE",FACE,{"disambiguationData":[OSD([sQuery(id+"F25.wireOp",EDGE,"E113.right")])]})});
            var sketch = newSketch(context, id + "F51", { "sketchPlane" : qUnion([Q0])});
            skCircle(sketch, "E158", {"center": v(-107.62, 49.36) * mm, "radius": 3.18 * mm});
            skLineSegment(sketch, "E159", {"start": v(-166.07, 49.36) * mm, "end": v(27.03, 49.36) * mm, "construction": true});
            skSolve(sketch);
        }
        {
            var Q0;
            Q0 = qSketchRegion(id + "F51", true);
            extrude(context, id + "F52", {"entities" : qUnion([Q0]), "operationType" : NewBodyOperationType.REMOVE, "endBound" : BoundingType.THROUGH_ALL, "oppositeDirection" : true, "depth" : 25.4 * mm});
        }
    });
